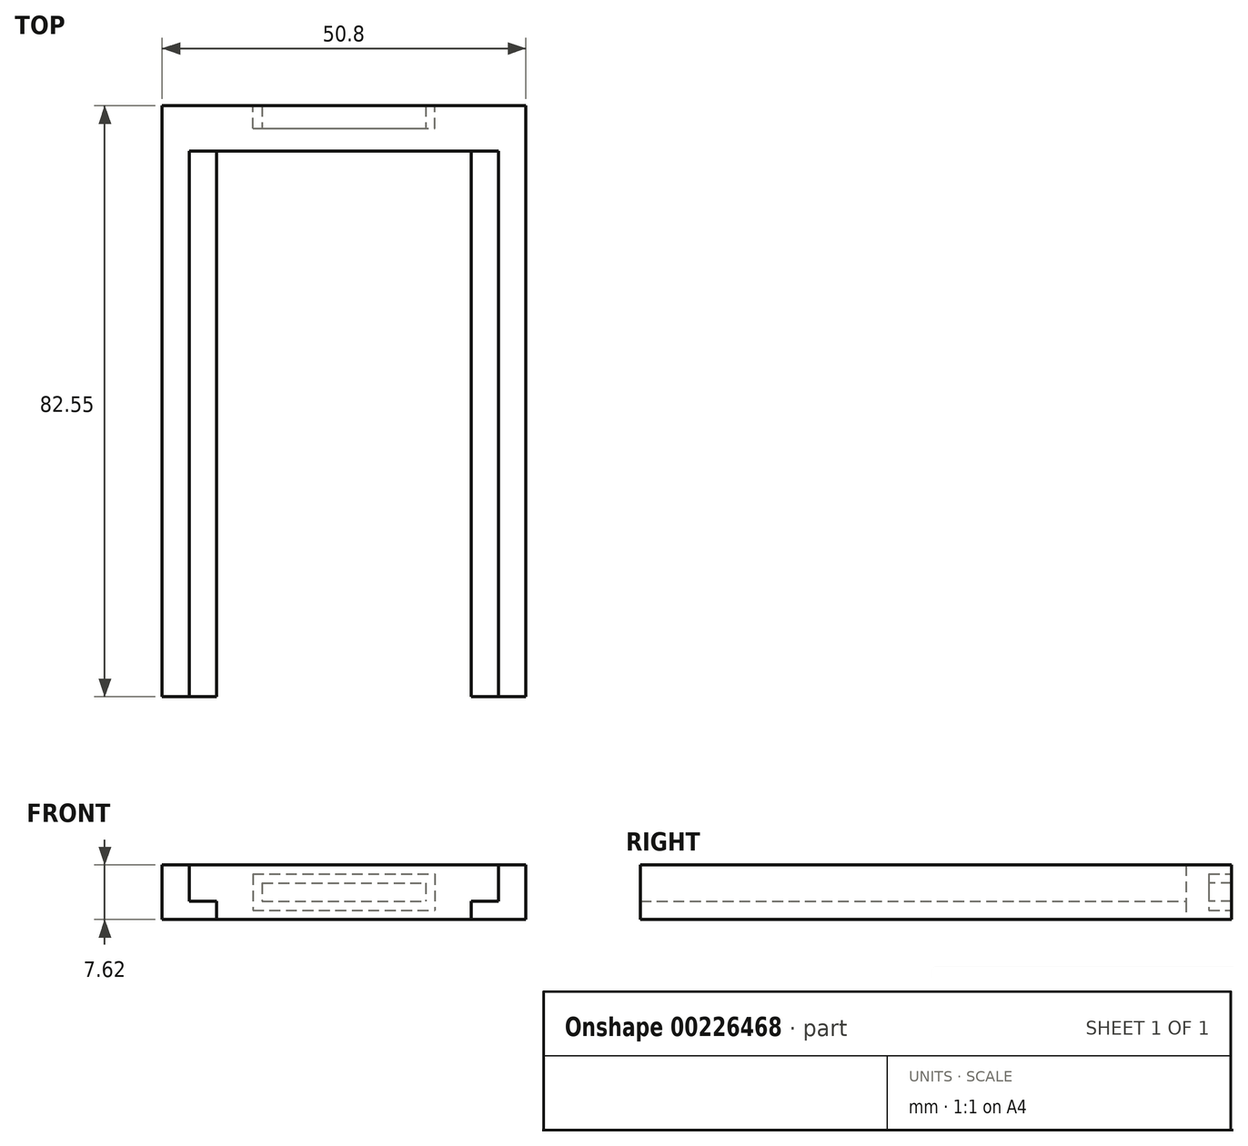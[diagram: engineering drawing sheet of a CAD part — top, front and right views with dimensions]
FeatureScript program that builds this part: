
annotation { "Feature Type Name" : "Feature", "Feature Type Description" : "" }
export const myFeature = defineFeature(function(context is Context, id is Id, definition is map)
    precondition{}
    {
        {
            var Q0;
            Q0=qCreatedBy(makeId("Front.planeOp"),FACE);
            var sketch = newSketch(context, id + "F0", { "sketchPlane" : qUnion([Q0])});
            skLineSegment(sketch, "E0.bottom", {"start": v(25.4, 3.81) * mm, "end": v(-25.4, 3.81) * mm});
            skLineSegment(sketch, "E0.top", {"start": v(25.4, -3.81) * mm, "end": v(-25.4, -3.81) * mm});
            skLineSegment(sketch, "E0.left", {"start": v(25.4, 3.81) * mm, "end": v(25.4, -3.81) * mm});
            skLineSegment(sketch, "E0.right", {"start": v(-25.4, 3.81) * mm, "end": v(-25.4, -3.81) * mm});
            skPoint(sketch, "E0.middle", {"position": v(0, 0) * mm});
            skSolve(sketch);
        }
        {
            var Q0;
            Q0=makeQuery(id+"F0.imprint","IMPRINT",FACE,{"disambiguationData":[TD([[makeQuery(id+"F0.imprint","IMPRINT",EDGE,{"derivedFrom":sQuery(id+"F0.wireOp",EDGE,"E0.bottom")}),1.0]])]});
            extrude(context, id + "F1", {"entities" : qUnion([Q0]), "depth" : 6.35 * mm});
        }
        {
            var Q0;
            Q0=makeQuery(id+"F1.opExtrude","CAP_FACE",FACE,{"disambiguationData":[OSD([sQuery(id+"F0.wireOp",EDGE,"E0.bottom"),sQuery(id+"F0.wireOp",EDGE,"E0.top"),sQuery(id+"F0.wireOp",EDGE,"E0.left"),sQuery(id+"F0.wireOp",EDGE,"E0.right")])],"isStart":false});
            var sketch = newSketch(context, id + "F2", { "sketchPlane" : qUnion([Q0])});
            skLineSegment(sketch, "E1", {"start": v(-21.59, 3.81) * mm, "end": v(-21.59, -1.27) * mm});
            skLineSegment(sketch, "E2", {"start": v(-21.59, -1.27) * mm, "end": v(-17.78, -1.27) * mm});
            skLineSegment(sketch, "E3", {"start": v(-17.78, -1.27) * mm, "end": v(-17.78, -3.81) * mm});
            skLineSegment(sketch, "E4", {"start": v(-17.78, -3.81) * mm, "end": v(-25.4, -3.81) * mm});
            skLineSegment(sketch, "E5", {"start": v(-25.4, 3.81) * mm, "end": v(-25.4, -3.81) * mm});
            skLineSegment(sketch, "E6", {"start": v(-25.4, 3.81) * mm, "end": v(-21.59, 3.81) * mm});
            skLineSegment(sketch, "E7.MirrorCS", {"start": v(17.78, -1.27) * mm, "end": v(17.78, -3.81) * mm});
            skLineSegment(sketch, "E8.MirrorCS", {"start": v(21.59, -1.27) * mm, "end": v(17.78, -1.27) * mm});
            skLineSegment(sketch, "E9.MirrorCS", {"start": v(25.4, 3.81) * mm, "end": v(21.59, 3.81) * mm});
            skLineSegment(sketch, "E10.MirrorCS", {"start": v(25.4, 3.81) * mm, "end": v(25.4, -3.81) * mm});
            skLineSegment(sketch, "E11.MirrorCS", {"start": v(17.78, -3.81) * mm, "end": v(25.4, -3.81) * mm});
            skLineSegment(sketch, "E12.MirrorCS", {"start": v(21.59, 3.81) * mm, "end": v(21.59, -1.27) * mm});
            skSolve(sketch);
        }
        {
            var Q0;
            Q0=makeQuery(id+"F2.imprint","IMPRINT",FACE,{"disambiguationData":[TD([[makeQuery(id+"F2.imprint","IMPRINT",EDGE,{"derivedFrom":sQuery(id+"F2.wireOp",EDGE,"E1")}),-1.0]])]});
            var Q1;
            Q1=makeQuery(id+"F2.imprint","IMPRINT",FACE,{"disambiguationData":[TD([[makeQuery(id+"F2.imprint","IMPRINT",EDGE,{"derivedFrom":sQuery(id+"F2.wireOp",EDGE,"E7.MirrorCS")}),1.0]])]});
            extrude(context, id + "F3", {"entities" : qUnion([Q0, Q1]), "operationType" : NewBodyOperationType.ADD, "depth" : 76.2 * mm});
        }
        {
            var Q0;
            Q0=makeQuery(id+"F1.opExtrude","CAP_FACE",FACE,{"disambiguationData":[OSD([sQuery(id+"F0.wireOp",EDGE,"E0.bottom"),sQuery(id+"F0.wireOp",EDGE,"E0.top"),sQuery(id+"F0.wireOp",EDGE,"E0.left"),sQuery(id+"F0.wireOp",EDGE,"E0.right")])],"isStart":true});
            var sketch = newSketch(context, id + "F4", { "sketchPlane" : qUnion([Q0])});
            skLineSegment(sketch, "E13.bottom", {"start": v(12.7, 2.54) * mm, "end": v(-12.7, 2.54) * mm});
            skLineSegment(sketch, "E13.top", {"start": v(12.7, -2.54) * mm, "end": v(-12.7, -2.54) * mm});
            skLineSegment(sketch, "E13.left", {"start": v(12.7, 2.54) * mm, "end": v(12.7, -2.54) * mm});
            skLineSegment(sketch, "E13.right", {"start": v(-12.7, 2.54) * mm, "end": v(-12.7, -2.54) * mm});
            skPoint(sketch, "E13.middle", {"position": v(0, 0) * mm});
            skSolve(sketch);
        }
        {
            var Q0;
            Q0=makeQuery(id+"F4.imprint","IMPRINT",FACE,{"disambiguationData":[TD([[makeQuery(id+"F4.imprint","IMPRINT",EDGE,{"derivedFrom":sQuery(id+"F4.wireOp",EDGE,"E13.bottom")}),1.0]])]});
            extrude(context, id + "F5", {"entities" : qUnion([Q0]), "operationType" : NewBodyOperationType.REMOVE, "oppositeDirection" : true, "depth" : 3.17 * mm});
        }
        {
            var Q0;
            Q0=makeQuery(id+"F5.boolean.opBoolean","COPY",FACE,{"derivedFrom":makeQuery(id+"F5.opExtrude","CAP_FACE",FACE,{"disambiguationData":[OSD([sQuery(id+"F4.wireOp",EDGE,"E13.bottom"),sQuery(id+"F4.wireOp",EDGE,"E13.top"),sQuery(id+"F4.wireOp",EDGE,"E13.left"),sQuery(id+"F4.wireOp",EDGE,"E13.right")])],"isStart":false})});
            var sketch = newSketch(context, id + "F6", { "sketchPlane" : qUnion([Q0])});
            skLineSegment(sketch, "E14.0", {"start": v(12.7, 2.54) * mm, "end": v(12.7, -2.54) * mm});
            skLineSegment(sketch, "E14.1", {"start": v(12.7, 2.54) * mm, "end": v(-12.7, 2.54) * mm});
            skLineSegment(sketch, "E14.2", {"start": v(-12.7, 2.54) * mm, "end": v(-12.7, -2.54) * mm});
            skLineSegment(sketch, "E14.3", {"start": v(12.7, -2.54) * mm, "end": v(-12.7, -2.54) * mm});
            skLineSegment(sketch, "E15.0", {"start": v(11.43, 1.27) * mm, "end": v(-11.43, 1.27) * mm});
            skLineSegment(sketch, "E15.1", {"start": v(11.43, 1.27) * mm, "end": v(11.43, -1.27) * mm});
            skLineSegment(sketch, "E15.2", {"start": v(11.43, -1.27) * mm, "end": v(-11.43, -1.27) * mm});
            skLineSegment(sketch, "E15.3", {"start": v(-11.43, 1.27) * mm, "end": v(-11.43, -1.27) * mm});
            skSolve(sketch);
        }
        {
            var Q0;
            Q0=makeQuery(id+"F6.imprint","IMPRINT",FACE,{"disambiguationData":[TD([[makeQuery(id+"F6.imprint","IMPRINT",EDGE,{"derivedFrom":sQuery(id+"F6.wireOp",EDGE,"E15.0")}),1.0]])]});
            extrude(context, id + "F7", {"entities" : qUnion([Q0]), "depth" : 3.17 * mm});
        }
    });
